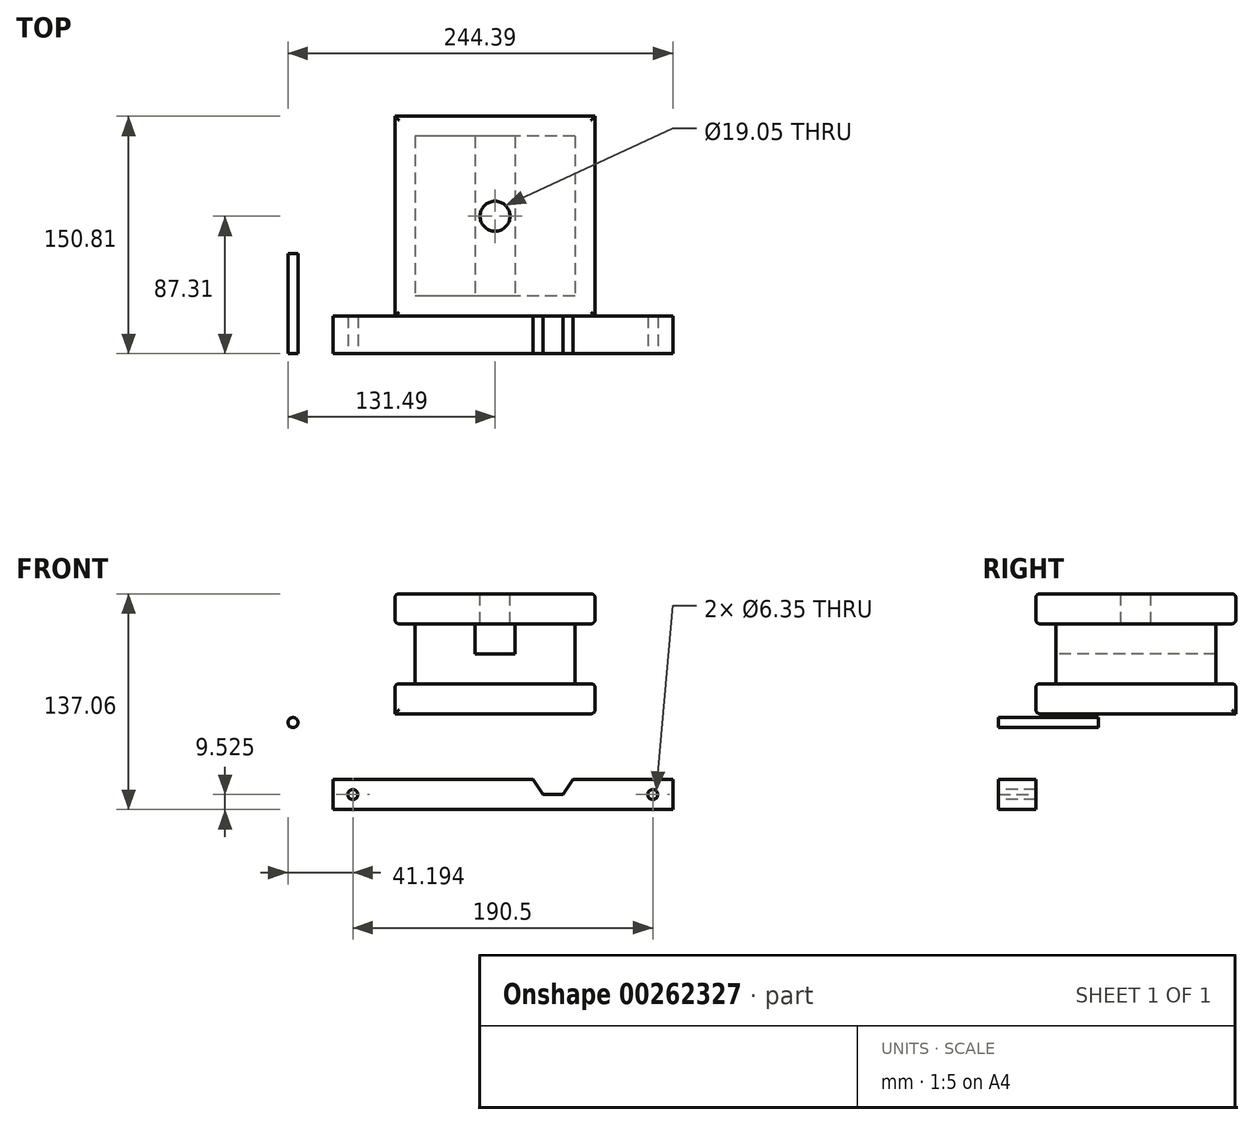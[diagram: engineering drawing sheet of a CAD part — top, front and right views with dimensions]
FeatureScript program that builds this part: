
annotation { "Feature Type Name" : "Feature", "Feature Type Description" : "" }
export const myFeature = defineFeature(function(context is Context, id is Id, definition is map)
    precondition{}
    {
        {
            var Q0;
            Q0=qCreatedBy(makeId("Top.planeOp"),FACE);
            var sketch = newSketch(context, id + "F0", { "sketchPlane" : qUnion([Q0])});
            skLineSegment(sketch, "E0.bottom", {"start": v(63.5, -63.5) * mm, "end": v(-63.5, -63.5) * mm});
            skLineSegment(sketch, "E0.top", {"start": v(63.5, 63.5) * mm, "end": v(-63.5, 63.5) * mm});
            skLineSegment(sketch, "E0.left", {"start": v(63.5, -63.5) * mm, "end": v(63.5, 63.5) * mm});
            skLineSegment(sketch, "E0.right", {"start": v(-63.5, -63.5) * mm, "end": v(-63.5, 63.5) * mm});
            skPoint(sketch, "E0.middle", {"position": v(0, 0) * mm});
            skSolve(sketch);
        }
        {
            var Q0;
            Q0=makeQuery(id+"F0.imprint","IMPRINT",FACE,{"disambiguationData":[TD([[makeQuery(id+"F0.imprint","IMPRINT",EDGE,{"derivedFrom":sQuery(id+"F0.wireOp",EDGE,"E0.bottom")}),-1.0]])]});
            extrude(context, id + "F1", {"entities" : qUnion([Q0]), "depth" : 19.05 * mm});
        }
        {
            var Q0;
            Q0=makeQuery(id+"F1.opExtrude","CAP_FACE",FACE,{"disambiguationData":[OSD([sQuery(id+"F0.wireOp",EDGE,"E0.bottom"),sQuery(id+"F0.wireOp",EDGE,"E0.top"),sQuery(id+"F0.wireOp",EDGE,"E0.left"),sQuery(id+"F0.wireOp",EDGE,"E0.right")])],"isStart":false});
            var sketch = newSketch(context, id + "F2", { "sketchPlane" : qUnion([Q0])});
            skLineSegment(sketch, "E1.bottom", {"start": v(50.8, 50.8) * mm, "end": v(-50.8, 50.8) * mm});
            skLineSegment(sketch, "E1.top", {"start": v(50.8, -50.8) * mm, "end": v(-50.8, -50.8) * mm});
            skLineSegment(sketch, "E1.left", {"start": v(50.8, 50.8) * mm, "end": v(50.8, -50.8) * mm});
            skLineSegment(sketch, "E1.right", {"start": v(-50.8, 50.8) * mm, "end": v(-50.8, -50.8) * mm});
            skPoint(sketch, "E1.middle", {"position": v(0, 0) * mm});
            skSolve(sketch);
        }
        {
            var Q0;
            Q0=makeQuery(id+"F2.imprint","IMPRINT",FACE,{"disambiguationData":[TD([[makeQuery(id+"F2.imprint","IMPRINT",EDGE,{"derivedFrom":sQuery(id+"F2.wireOp",EDGE,"E1.bottom")}),1.0]])]});
            extrude(context, id + "F3", {"entities" : qUnion([Q0]), "operationType" : NewBodyOperationType.ADD, "depth" : 38.1 * mm});
        }
        {
            var Q0;
            Q0=makeQuery(id+"F3.opExtrude","CAP_FACE",FACE,{"disambiguationData":[OSD([sQuery(id+"F2.wireOp",EDGE,"E1.bottom"),sQuery(id+"F2.wireOp",EDGE,"E1.top"),sQuery(id+"F2.wireOp",EDGE,"E1.left"),sQuery(id+"F2.wireOp",EDGE,"E1.right")])],"isStart":false});
            var sketch = newSketch(context, id + "F4", { "sketchPlane" : qUnion([Q0])});
            skLineSegment(sketch, "E2.bottom", {"start": v(63.5, -63.5) * mm, "end": v(-63.5, -63.5) * mm});
            skLineSegment(sketch, "E2.top", {"start": v(63.5, 63.5) * mm, "end": v(-63.5, 63.5) * mm});
            skLineSegment(sketch, "E2.left", {"start": v(63.5, -63.5) * mm, "end": v(63.5, 63.5) * mm});
            skLineSegment(sketch, "E2.right", {"start": v(-63.5, -63.5) * mm, "end": v(-63.5, 63.5) * mm});
            skPoint(sketch, "E2.middle", {"position": v(0, 0) * mm});
            skSolve(sketch);
        }
        {
            var Q0;
            Q0=makeQuery(id+"F4.imprint","IMPRINT",FACE,{"disambiguationData":[TD([[makeQuery(id+"F4.imprint","IMPRINT",EDGE,{"derivedFrom":sQuery(id+"F4.wireOp",EDGE,"E2.bottom")}),-1.0]])]});
            var Q1;
            Q1=makeQuery(id+"F4.imprint","IMPRINT",FACE,{"disambiguationData":[TD([[makeQuery(id+"F4.imprint","IMPRINT",EDGE,{"derivedFrom":makeQuery(id+"F3.opExtrude","CAP_EDGE",EDGE,{"disambiguationData":[OSD([sQuery(id+"F2.wireOp",EDGE,"E1.bottom")])],"isStart":false})}),1.0]])]});
            extrude(context, id + "F5", {"entities" : qUnion([Q0, Q1]), "operationType" : NewBodyOperationType.ADD, "depth" : 19.05 * mm});
        }
        {
            var Q0;
            Q0=makeQuery(id+"F3.opExtrude","SWEPT_FACE",FACE,{"disambiguationData":[OSD([sQuery(id+"F2.wireOp",EDGE,"E1.top")])]});
            var sketch = newSketch(context, id + "F6", { "sketchPlane" : qUnion([Q0])});
            skLineSegment(sketch, "E3", {"start": v(0, 19.05) * mm, "end": v(0, 38.1) * mm});
            skPoint(sketch, "E3.endSnap0", {"position": v(0, 19.05) * mm});
            skLineSegment(sketch, "E4", {"start": v(0, 38.1) * mm, "end": v(0, 47.62) * mm});
            skLineSegment(sketch, "E5.bottom", {"start": v(12.7, 57.15) * mm, "end": v(-12.7, 57.15) * mm});
            skLineSegment(sketch, "E5.top", {"start": v(12.7, 38.1) * mm, "end": v(-12.7, 38.1) * mm});
            skLineSegment(sketch, "E5.left", {"start": v(12.7, 57.15) * mm, "end": v(12.7, 38.1) * mm});
            skLineSegment(sketch, "E5.right", {"start": v(-12.7, 57.15) * mm, "end": v(-12.7, 38.1) * mm});
            skPoint(sketch, "E5.middle", {"position": v(0, 47.62) * mm});
            skSolve(sketch);
        }
        {
            var Q0;
            Q0=makeQuery(id+"F6.imprint","IMPRINT",FACE,{"disambiguationData":[TD([[makeQuery(id+"F6.imprint","IMPRINT",EDGE,{"derivedFrom":sQuery(id+"F6.wireOp",EDGE,"E5.bottom")}),1.0]])]});
            extrude(context, id + "F7", {"entities" : qUnion([Q0]), "operationType" : NewBodyOperationType.REMOVE, "oppositeDirection" : true, "depth" : 101.6 * mm});
        }
        {
            var Q0;
            Q0=makeQuery(id+"F5.opExtrude","CAP_FACE",FACE,{"disambiguationData":[OSD([sQuery(id+"F4.wireOp",EDGE,"E2.bottom"),sQuery(id+"F4.wireOp",EDGE,"E2.top"),sQuery(id+"F4.wireOp",EDGE,"E2.left"),sQuery(id+"F4.wireOp",EDGE,"E2.right")])],"isStart":false});
            var sketch = newSketch(context, id + "F8", { "sketchPlane" : qUnion([Q0])});
            skLineSegment(sketch, "E6", {"start": v(0, -63.5) * mm, "end": v(0, 0) * mm});
            skPoint(sketch, "E6.endSnap0", {"position": v(0, -63.5) * mm});
            skSolve(sketch);
        }
        {
            var Q0;
            Q0=sQuery(id+"F8.wireOp",VERTEX,"E6.end");
            var Q1;
            Q1=makeQuery(id+"F1.opExtrude","SWEPT_BODY",BODY,{"disambiguationData":[OSD([sQuery(id+"F0.wireOp",EDGE,"E0.bottom"),sQuery(id+"F0.wireOp",EDGE,"E0.top"),sQuery(id+"F0.wireOp",EDGE,"E0.left"),sQuery(id+"F0.wireOp",EDGE,"E0.right")])]});
            hole(context, id + "F9", {"style" : HoleStyle.SIMPLE, "endStyle" : HoleEndStyle.BLIND, "holeDiameter" : 19.05 * mm, "holeDepth" : 19.05 * mm, "tappedDepth" : 12.7 * mm, "tapClearance" : 3, "startFromSketch" : true, "locations" : qUnion([Q0]), "scope" : qUnion([Q1])});
        }
        {
            var Q0;
            Q0=makeQuery(id+"F5.opExtrude","CAP_EDGE",EDGE,{"disambiguationData":[OSD([sQuery(id+"F4.wireOp",EDGE,"E2.right")])],"isStart":false});
            var Q1;
            Q1=makeQuery(id+"F5.opExtrude","CAP_EDGE",EDGE,{"disambiguationData":[OSD([sQuery(id+"F4.wireOp",EDGE,"E2.top")])],"isStart":false});
            var Q2;
            Q2=makeQuery(id+"F5.opExtrude","CAP_EDGE",EDGE,{"disambiguationData":[OSD([sQuery(id+"F4.wireOp",EDGE,"E2.left")])],"isStart":false});
            var Q3;
            Q3=makeQuery(id+"F5.opExtrude","CAP_EDGE",EDGE,{"disambiguationData":[OSD([sQuery(id+"F4.wireOp",EDGE,"E2.bottom")])],"isStart":false});
            fillet(context, id + "F10", {"entities" : qUnion([Q0, Q1, Q2, Q3]), "radius" : 2.54 * mm, "tangentPropagation" : true, "allowEdgeOverflow" : false});
        }
        {
            var Q0;
            Q0=makeQuery(id+"F5.opExtrude","CAP_EDGE",EDGE,{"disambiguationData":[OSD([sQuery(id+"F4.wireOp",EDGE,"E2.bottom")])],"isStart":true});
            var Q1;
            Q1=makeQuery(id+"F5.opExtrude","CAP_EDGE",EDGE,{"disambiguationData":[OSD([sQuery(id+"F4.wireOp",EDGE,"E2.left")])],"isStart":true});
            var Q2;
            Q2=makeQuery(id+"F5.opExtrude","CAP_EDGE",EDGE,{"disambiguationData":[OSD([sQuery(id+"F4.wireOp",EDGE,"E2.top")])],"isStart":true});
            var Q3;
            Q3=makeQuery(id+"F5.opExtrude","CAP_EDGE",EDGE,{"disambiguationData":[OSD([sQuery(id+"F4.wireOp",EDGE,"E2.right")])],"isStart":true});
            fillet(context, id + "F11", {"entities" : qUnion([Q0, Q1, Q2, Q3]), "radius" : 2.54 * mm, "tangentPropagation" : true, "allowEdgeOverflow" : false});
        }
        {
            var Q0;
            Q0=makeQuery(id+"F1.opExtrude","CAP_EDGE",EDGE,{"disambiguationData":[OSD([sQuery(id+"F0.wireOp",EDGE,"E0.right")])],"isStart":false});
            var Q1;
            Q1=makeQuery(id+"F1.opExtrude","CAP_EDGE",EDGE,{"disambiguationData":[OSD([sQuery(id+"F0.wireOp",EDGE,"E0.top")])],"isStart":false});
            var Q2;
            Q2=makeQuery(id+"F1.opExtrude","SWEPT_FACE",FACE,{"disambiguationData":[OSD([sQuery(id+"F0.wireOp",EDGE,"E0.left")])]});
            var Q3;
            Q3=makeQuery(id+"F1.opExtrude","SWEPT_FACE",FACE,{"disambiguationData":[OSD([sQuery(id+"F0.wireOp",EDGE,"E0.bottom")])]});
            fillet(context, id + "F12", {"entities" : qUnion([Q0, Q1, Q2, Q3]), "radius" : 2.54 * mm, "tangentPropagation" : true, "allowEdgeOverflow" : false});
        }
        {
            var Q0;
            Q0=makeQuery(id+"F1.opExtrude","SWEPT_FACE",FACE,{"disambiguationData":[OSD([sQuery(id+"F0.wireOp",EDGE,"E0.bottom")])]});
            var sketch = newSketch(context, id + "F13", { "sketchPlane" : qUnion([Q0])});
            skLineSegment(sketch, "E7.bottom", {"start": v(-103, -60.86) * mm, "end": v(112.9, -60.86) * mm});
            skLineSegment(sketch, "E7.top", {"start": v(-103, -41.81) * mm, "end": v(24, -41.81) * mm});
            skLineSegment(sketch, "E7.left", {"start": v(-103, -60.86) * mm, "end": v(-103, -41.81) * mm});
            skLineSegment(sketch, "E7.right", {"start": v(112.9, -60.86) * mm, "end": v(112.9, -41.81) * mm});
            skLineSegment(sketch, "E8", {"start": v(112.9, -41.81) * mm, "end": v(49.4, -41.81) * mm});
            skLineSegment(sketch, "E9", {"start": v(36.7, -51.34) * mm, "end": v(30.35, -51.34) * mm});
            skLineSegment(sketch, "E10", {"start": v(36.7, -51.34) * mm, "end": v(43.05, -51.34) * mm});
            skLineSegment(sketch, "E11", {"start": v(30.35, -51.34) * mm, "end": v(24, -41.81) * mm});
            skLineSegment(sketch, "E12", {"start": v(43.05, -51.34) * mm, "end": v(49.4, -41.81) * mm});
            skPoint(sketch, "E13.start.orphan", {"position": v(36.7, -41.81) * mm});
            skLineSegment(sketch, "E14.trimOffspring", {"start": v(49.4, -41.81) * mm, "end": v(112.9, -41.81) * mm});
            skSolve(sketch);
        }
        {
            var Q0;
            Q0=makeQuery(id+"F13.imprint","IMPRINT",FACE,{"disambiguationData":[TD([[makeQuery(id+"F13.imprint","IMPRINT",EDGE,{"derivedFrom":sQuery(id+"F13.wireOp",EDGE,"E7.bottom")}),1.0]])]});
            extrude(context, id + "F14", {"entities" : qUnion([Q0]), "depth" : 23.8 * mm});
        }
        {
            var Q0;
            Q0=makeQuery(id+"F14.opExtrude","CAP_FACE",FACE,{"disambiguationData":[OSD([sQuery(id+"F13.wireOp",EDGE,"E7.bottom"),sQuery(id+"F13.wireOp",EDGE,"E7.top"),sQuery(id+"F13.wireOp",EDGE,"E7.left"),sQuery(id+"F13.wireOp",EDGE,"E7.right"),sQuery(id+"F13.wireOp",EDGE,"E9"),sQuery(id+"F13.wireOp",EDGE,"E10"),sQuery(id+"F13.wireOp",EDGE,"E11"),sQuery(id+"F13.wireOp",EDGE,"E12"),sQuery(id+"F13.wireOp",EDGE,"E14.trimOffspring")])],"isStart":false});
            var sketch = newSketch(context, id + "F15", { "sketchPlane" : qUnion([Q0])});
            skLineSegment(sketch, "E15", {"start": v(-103, -41.81) * mm, "end": v(-90.3, -41.81) * mm});
            skLineSegment(sketch, "E16", {"start": v(-90.3, -41.81) * mm, "end": v(-90.3, -51.34) * mm});
            skLineSegment(sketch, "E17", {"start": v(112.9, -41.81) * mm, "end": v(100.2, -41.81) * mm});
            skLineSegment(sketch, "E18", {"start": v(100.2, -41.81) * mm, "end": v(100.2, -51.34) * mm});
            skSolve(sketch);
        }
        {
            var Q0;
            Q0=sQuery(id+"F15.wireOp",VERTEX,"E16.end");
            var Q1;
            Q1=sQuery(id+"F15.wireOp",VERTEX,"E18.end");
            var Q2;
            Q2=makeQuery(id+"F14.opExtrude","SWEPT_BODY",BODY,{"disambiguationData":[OSD([sQuery(id+"F13.wireOp",EDGE,"E7.bottom"),sQuery(id+"F13.wireOp",EDGE,"E7.top"),sQuery(id+"F13.wireOp",EDGE,"E7.left"),sQuery(id+"F13.wireOp",EDGE,"E7.right"),sQuery(id+"F13.wireOp",EDGE,"E9"),sQuery(id+"F13.wireOp",EDGE,"E10"),sQuery(id+"F13.wireOp",EDGE,"E11"),sQuery(id+"F13.wireOp",EDGE,"E12"),sQuery(id+"F13.wireOp",EDGE,"E14.trimOffspring")])]});
            hole(context, id + "F16", {"style" : HoleStyle.SIMPLE, "endStyle" : HoleEndStyle.THROUGH, "holeDiameter" : 6.35 * mm, "tappedDepth" : 12.7 * mm, "tapClearance" : 3, "startFromSketch" : true, "locations" : qUnion([Q0, Q1]), "scope" : qUnion([Q2])});
        }
        {
            var Q0;
            Q0=makeQuery(id+"F14.opExtrude","CAP_FACE",FACE,{"disambiguationData":[OSD([sQuery(id+"F13.wireOp",EDGE,"E7.bottom"),sQuery(id+"F13.wireOp",EDGE,"E7.top"),sQuery(id+"F13.wireOp",EDGE,"E7.left"),sQuery(id+"F13.wireOp",EDGE,"E7.right"),sQuery(id+"F13.wireOp",EDGE,"E9"),sQuery(id+"F13.wireOp",EDGE,"E10"),sQuery(id+"F13.wireOp",EDGE,"E11"),sQuery(id+"F13.wireOp",EDGE,"E12"),sQuery(id+"F13.wireOp",EDGE,"E14.trimOffspring")])],"isStart":false});
            var sketch = newSketch(context, id + "F17", { "sketchPlane" : qUnion([Q0])});
            skCircle(sketch, "E19", {"center": v(-128.32, -5.6) * mm, "radius": 3.18 * mm});
            skSolve(sketch);
        }
        {
            var Q0;
            Q0=makeQuery(id+"F17.imprint","IMPRINT",FACE,{"disambiguationData":[TD([[makeQuery(id+"F17.imprint","IMPRINT",EDGE,{"derivedFrom":sQuery(id+"F17.wireOp",EDGE,"E19")}),1.0]])]});
            extrude(context, id + "F18", {"entities" : qUnion([Q0]), "oppositeDirection" : true, "depth" : 63.5 * mm});
        }
        {
            var Q0;
            Q0=qCreatedBy(makeId("Top.planeOp"),FACE);
            var sketch = newSketch(context, id + "F19", { "sketchPlane" : qUnion([Q0])});
            skLineSegment(sketch, "E20.bottom", {"start": v(-44.76, -340.9) * mm, "end": v(-82.86, -340.9) * mm});
            skLineSegment(sketch, "E20.top", {"start": v(-44.76, -264.7) * mm, "end": v(-82.86, -264.7) * mm});
            skLineSegment(sketch, "E20.left", {"start": v(-25.71, -321.84) * mm, "end": v(-25.71, -283.74) * mm});
            skLineSegment(sketch, "E20.right", {"start": v(-101.91, -321.84) * mm, "end": v(-101.91, -283.74) * mm});
            skPoint(sketch, "E20.middle", {"position": v(-63.81, -302.8) * mm});
            skPoint(sketch, "E21.visualSharp", {"position": v(-101.91, -340.9) * mm});
            skArc(sketch, "E21.filletArc", {"start": v(-101.91, -321.84) * mm, "mid": v(-96.33, -335.31) * mm, "end": v(-82.86, -340.9) * mm});
            skPoint(sketch, "E22.visualSharp", {"position": v(-101.91, -264.7) * mm});
            skArc(sketch, "E22.filletArc", {"start": v(-82.86, -264.7) * mm, "mid": v(-96.33, -270.27) * mm, "end": v(-101.91, -283.74) * mm});
            skPoint(sketch, "E23.visualSharp", {"position": v(-25.71, -264.7) * mm});
            skArc(sketch, "E23.filletArc", {"start": v(-25.71, -283.74) * mm, "mid": v(-31.3, -270.27) * mm, "end": v(-44.76, -264.7) * mm});
            skPoint(sketch, "E24.visualSharp", {"position": v(-25.71, -340.9) * mm});
            skArc(sketch, "E24.filletArc", {"start": v(-44.76, -340.9) * mm, "mid": v(-31.3, -335.31) * mm, "end": v(-25.71, -321.84) * mm});
            skSolve(sketch);
        }
        {
            var Q0;
            Q0=makeQuery(id+"F19.imprint","IMPRINT",FACE,{"disambiguationData":[TD([[makeQuery(id+"F19.imprint","IMPRINT",EDGE,{"derivedFrom":sQuery(id+"F19.wireOp",EDGE,"E20.bottom")}),-1.0]])]});
            extrude(context, id + "F20", {"entities" : qUnion([Q0]), "depth" : 101.6 * mm});
        }
        {
            var Q0;
            Q0=makeQuery(id+"F20.opExtrude","CAP_FACE",FACE,{"disambiguationData":[OSD([sQuery(id+"F19.wireOp",EDGE,"E20.bottom"),sQuery(id+"F19.wireOp",EDGE,"E20.top"),sQuery(id+"F19.wireOp",EDGE,"E20.left"),sQuery(id+"F19.wireOp",EDGE,"E20.right"),sQuery(id+"F19.wireOp",EDGE,"E21.filletArc"),sQuery(id+"F19.wireOp",EDGE,"E22.filletArc"),sQuery(id+"F19.wireOp",EDGE,"E23.filletArc"),sQuery(id+"F19.wireOp",EDGE,"E24.filletArc")])],"isStart":true});
            var sketch = newSketch(context, id + "F21", { "sketchPlane" : qUnion([Q0])});
            skCircle(sketch, "E25", {"center": v(-63.81, 302.8) * mm, "radius": 31.75 * mm});
            skPoint(sketch, "E26.start.orphan", {"position": v(-96.33, 270.27) * mm});
            skPoint(sketch, "E27.start.orphan", {"position": v(-96.33, 335.31) * mm});
            skPoint(sketch, "E28.trimOffspring.end.orphan", {"position": v(-31.3, 335.31) * mm});
            skPoint(sketch, "E29.trimOffspring.end.orphan", {"position": v(-31.3, 270.27) * mm});
            skSolve(sketch);
        }
        {
            var Q0;
            Q0=makeQuery(id+"F21.imprint","IMPRINT",FACE,{"disambiguationData":[TD([[makeQuery(id+"F21.imprint","IMPRINT",EDGE,{"derivedFrom":sQuery(id+"F21.wireOp",EDGE,"E25")}),1.0]])]});
            extrude(context, id + "F22", {"entities" : qUnion([Q0]), "operationType" : NewBodyOperationType.ADD, "depth" : 38.1 * mm});
        }
        {
            var Q0;
            Q0=makeQuery(id+"F20.opExtrude","SWEPT_BODY",BODY,{"disambiguationData":[OSD([sQuery(id+"F19.wireOp",EDGE,"E20.bottom"),sQuery(id+"F19.wireOp",EDGE,"E20.top"),sQuery(id+"F19.wireOp",EDGE,"E20.left"),sQuery(id+"F19.wireOp",EDGE,"E20.right"),sQuery(id+"F19.wireOp",EDGE,"E21.filletArc"),sQuery(id+"F19.wireOp",EDGE,"E22.filletArc"),sQuery(id+"F19.wireOp",EDGE,"E23.filletArc"),sQuery(id+"F19.wireOp",EDGE,"E24.filletArc")])]});
            deleteBodies(context, id + "F23", {"entities" : qUnion([Q0])});
        }
    });
